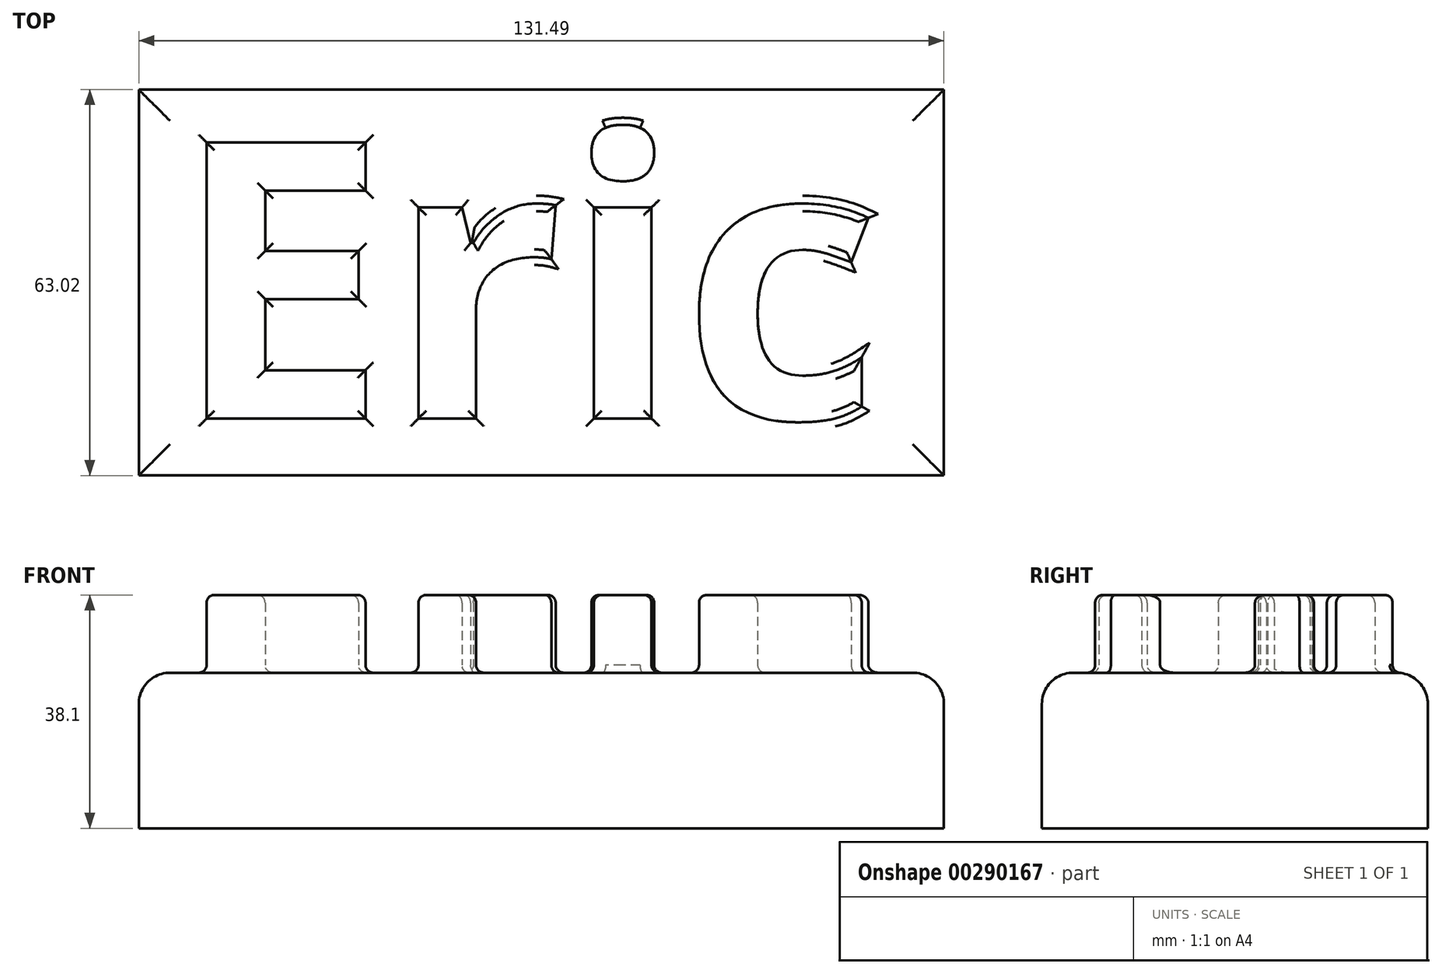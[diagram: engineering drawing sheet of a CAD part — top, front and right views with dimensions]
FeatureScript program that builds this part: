
annotation { "Feature Type Name" : "Feature", "Feature Type Description" : "" }
export const myFeature = defineFeature(function(context is Context, id is Id, definition is map)
    precondition{}
    {
        {
            var Q0;
            Q0=qCreatedBy(makeId("Top.planeOp"),FACE);
            var sketch = newSketch(context, id + "F0", { "sketchPlane" : qUnion([Q0])});
            skText(sketch, "E0", { "text": "Eric", "fontName": "OpenSans-Bold.ttf"});
            const initialGuessF0  = {"E0": [0, 0, 1, 0, 0.04544]};
            skSetInitialGuess(sketch, initialGuessF0);
            skSolve(sketch);
        }
        {
            var Q0;
            Q0=qCreatedBy(makeId("Top.planeOp"),FACE);
            var sketch = newSketch(context, id + "F1", { "sketchPlane" : qUnion([Q0])});
            skLineSegment(sketch, "E1.bottom", {"start": v(-5.4, -9.32) * mm, "end": v(126.09, -9.32) * mm});
            skLineSegment(sketch, "E1.top", {"start": v(-5.4, 53.7) * mm, "end": v(126.09, 53.7) * mm});
            skLineSegment(sketch, "E1.left", {"start": v(-5.4, -9.32) * mm, "end": v(-5.4, 53.7) * mm});
            skLineSegment(sketch, "E1.right", {"start": v(126.09, -9.32) * mm, "end": v(126.09, 53.7) * mm});
            skSolve(sketch);
        }
        {
            var Q0;
            Q0 = qSketchRegion(id + "F1", true);
            extrude(context, id + "F2", {"entities" : qUnion([Q0]), "oppositeDirection" : true, "depth" : 25.4 * mm});
        }
        {
            var Q0;
            Q0 = qSketchRegion(id + "F0", true);
            extrude(context, id + "F3", {"entities" : qUnion([Q0]), "operationType" : NewBodyOperationType.ADD, "depth" : 12.7 * mm});
        }
        {
            var Q0;
            Q0=makeQuery(id+"F2.opExtrude","CAP_EDGE",EDGE,{"disambiguationData":[OSD([sQuery(id+"F1.wireOp",EDGE,"E1.left")])],"isStart":true});
            var Q1;
            Q1=makeQuery(id+"F2.opExtrude","CAP_EDGE",EDGE,{"disambiguationData":[OSD([sQuery(id+"F1.wireOp",EDGE,"E1.bottom")])],"isStart":true});
            var Q2;
            Q2=makeQuery(id+"F2.opExtrude","CAP_EDGE",EDGE,{"disambiguationData":[OSD([sQuery(id+"F1.wireOp",EDGE,"E1.right")])],"isStart":true});
            var Q3;
            Q3=makeQuery(id+"F2.opExtrude","CAP_EDGE",EDGE,{"disambiguationData":[OSD([sQuery(id+"F1.wireOp",EDGE,"E1.top")])],"isStart":true});
            fillet(context, id + "F4", {"entities" : qUnion([Q0, Q1, Q2, Q3]), "radius" : 5.08 * mm, "tangentPropagation" : true, "allowEdgeOverflow" : false});
        }
        {
            var Q0;
            Q0=makeQuery(id+"F3.opExtrude","CAP_FACE",FACE,{"disambiguationData":[OSD([sQuery(id+"F0.wireOp",EDGE,"E0.sketch_text.stroke-0"),sQuery(id+"F0.wireOp",EDGE,"E0.sketch_text.stroke-1"),sQuery(id+"F0.wireOp",EDGE,"E0.sketch_text.stroke-2"),sQuery(id+"F0.wireOp",EDGE,"E0.sketch_text.stroke-3"),sQuery(id+"F0.wireOp",EDGE,"E0.sketch_text.stroke-4"),sQuery(id+"F0.wireOp",EDGE,"E0.sketch_text.stroke-5"),sQuery(id+"F0.wireOp",EDGE,"E0.sketch_text.stroke-6"),sQuery(id+"F0.wireOp",EDGE,"E0.sketch_text.stroke-7"),sQuery(id+"F0.wireOp",EDGE,"E0.sketch_text.stroke-8"),sQuery(id+"F0.wireOp",EDGE,"E0.sketch_text.stroke-9"),sQuery(id+"F0.wireOp",EDGE,"E0.sketch_text.stroke-10"),sQuery(id+"F0.wireOp",EDGE,"E0.sketch_text.stroke-11")])],"isStart":false});
            var Q1;
            Q1=makeQuery(id+"F3.opExtrude","CAP_FACE",FACE,{"disambiguationData":[OSD([sQuery(id+"F0.wireOp",EDGE,"E0.sketch_text.stroke-12"),sQuery(id+"F0.wireOp",EDGE,"E0.sketch_text.stroke-13"),sQuery(id+"F0.wireOp",EDGE,"E0.sketch_text.stroke-14"),sQuery(id+"F0.wireOp",EDGE,"E0.sketch_text.stroke-15"),sQuery(id+"F0.wireOp",EDGE,"E0.sketch_text.stroke-16"),sQuery(id+"F0.wireOp",EDGE,"E0.sketch_text.stroke-17"),sQuery(id+"F0.wireOp",EDGE,"E0.sketch_text.stroke-18"),sQuery(id+"F0.wireOp",EDGE,"E0.sketch_text.stroke-19"),sQuery(id+"F0.wireOp",EDGE,"E0.sketch_text.stroke-20"),sQuery(id+"F0.wireOp",EDGE,"E0.sketch_text.stroke-21"),sQuery(id+"F0.wireOp",EDGE,"E0.sketch_text.stroke-22"),sQuery(id+"F0.wireOp",EDGE,"E0.sketch_text.stroke-23"),sQuery(id+"F0.wireOp",EDGE,"E0.sketch_text.stroke-24")])],"isStart":false});
            var Q2;
            Q2=makeQuery(id+"F3.opExtrude","CAP_FACE",FACE,{"disambiguationData":[OSD([sQuery(id+"F0.wireOp",EDGE,"E0.sketch_text.stroke-30"),sQuery(id+"F0.wireOp",EDGE,"E0.sketch_text.stroke-31"),sQuery(id+"F0.wireOp",EDGE,"E0.sketch_text.stroke-32"),sQuery(id+"F0.wireOp",EDGE,"E0.sketch_text.stroke-33")])],"isStart":false});
            var Q3;
            Q3=makeQuery(id+"F3.opExtrude","CAP_FACE",FACE,{"disambiguationData":[OSD([sQuery(id+"F0.wireOp",EDGE,"E0.sketch_text.stroke-25"),sQuery(id+"F0.wireOp",EDGE,"E0.sketch_text.stroke-26"),sQuery(id+"F0.wireOp",EDGE,"E0.sketch_text.stroke-27"),sQuery(id+"F0.wireOp",EDGE,"E0.sketch_text.stroke-28"),sQuery(id+"F0.wireOp",EDGE,"E0.sketch_text.stroke-29")])],"isStart":false});
            var Q4;
            Q4=makeQuery(id+"F3.opExtrude","CAP_FACE",FACE,{"disambiguationData":[OSD([sQuery(id+"F0.wireOp",EDGE,"E0.sketch_text.stroke-34"),sQuery(id+"F0.wireOp",EDGE,"E0.sketch_text.stroke-35"),sQuery(id+"F0.wireOp",EDGE,"E0.sketch_text.stroke-36"),sQuery(id+"F0.wireOp",EDGE,"E0.sketch_text.stroke-37"),sQuery(id+"F0.wireOp",EDGE,"E0.sketch_text.stroke-38"),sQuery(id+"F0.wireOp",EDGE,"E0.sketch_text.stroke-39"),sQuery(id+"F0.wireOp",EDGE,"E0.sketch_text.stroke-40"),sQuery(id+"F0.wireOp",EDGE,"E0.sketch_text.stroke-41"),sQuery(id+"F0.wireOp",EDGE,"E0.sketch_text.stroke-42"),sQuery(id+"F0.wireOp",EDGE,"E0.sketch_text.stroke-43"),sQuery(id+"F0.wireOp",EDGE,"E0.sketch_text.stroke-44"),sQuery(id+"F0.wireOp",EDGE,"E0.sketch_text.stroke-45"),sQuery(id+"F0.wireOp",EDGE,"E0.sketch_text.stroke-46"),sQuery(id+"F0.wireOp",EDGE,"E0.sketch_text.stroke-47")])],"isStart":false});
            var Q5;
            Q5=makeQuery(id+"F2.opExtrude","CAP_FACE",FACE,{"disambiguationData":[OSD([sQuery(id+"F1.wireOp",EDGE,"E1.bottom"),sQuery(id+"F1.wireOp",EDGE,"E1.top"),sQuery(id+"F1.wireOp",EDGE,"E1.left"),sQuery(id+"F1.wireOp",EDGE,"E1.right")])],"isStart":true});
            fillet(context, id + "F5", {"entities" : qUnion([Q0, Q1, Q2, Q3, Q4, Q5]), "radius" : 1.27 * mm, "tangentPropagation" : true, "allowEdgeOverflow" : false});
        }
    });
